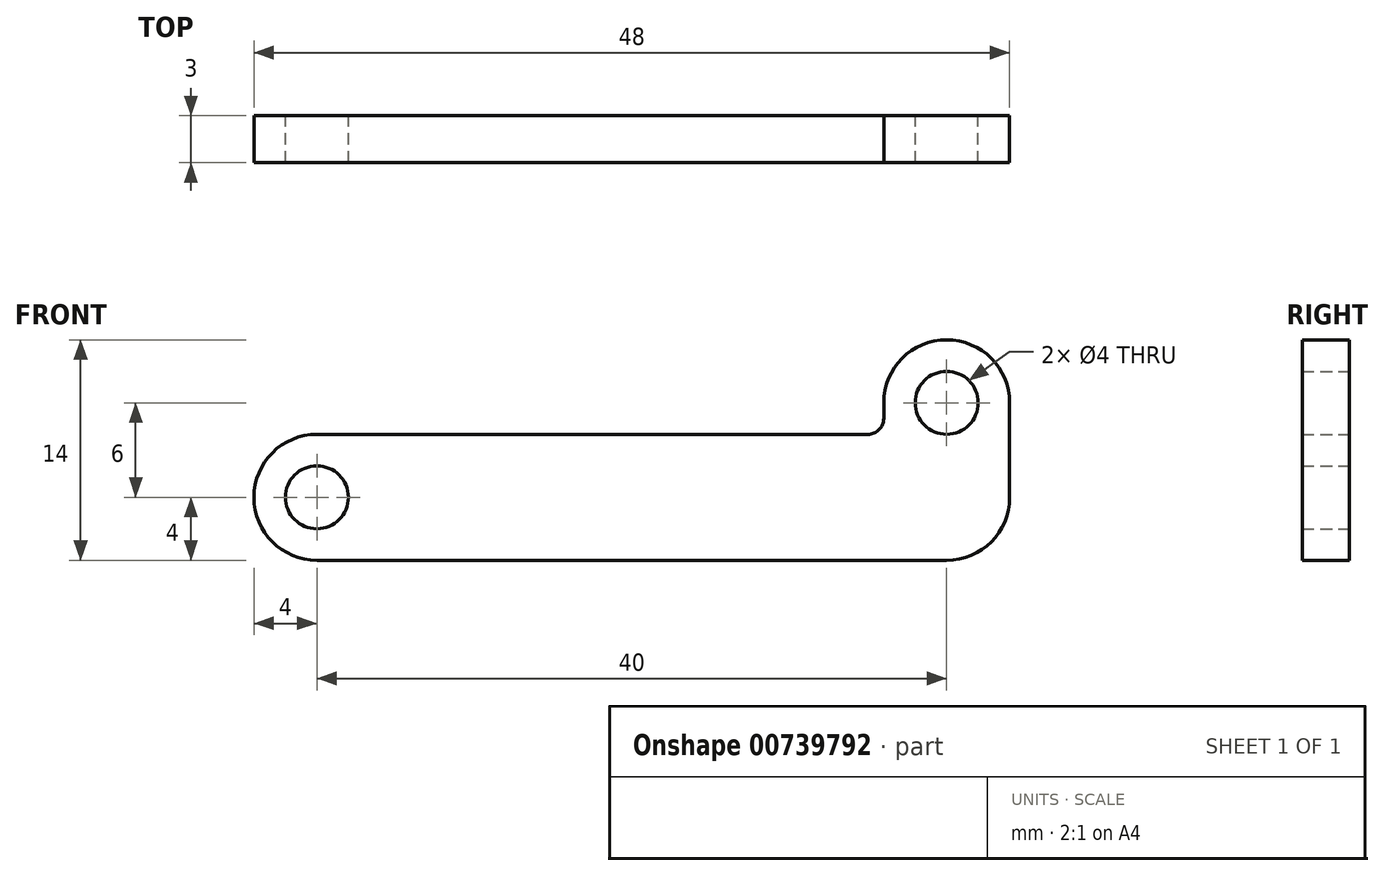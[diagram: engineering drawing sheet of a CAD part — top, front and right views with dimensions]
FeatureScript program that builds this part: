
annotation { "Feature Type Name" : "Feature", "Feature Type Description" : "" }
export const myFeature = defineFeature(function(context is Context, id is Id, definition is map)
    precondition{}
    {
        {
            var Q0;
            Q0=qCreatedBy(makeId("Front.planeOp"),FACE);
            var sketch = newSketch(context, id + "F0", { "sketchPlane" : qUnion([Q0])});
            skLineSegment(sketch, "E0.bottom", {"start": v(-40, 4) * mm, "end": v(-5, 4) * mm});
            skLineSegment(sketch, "E0.top", {"start": v(-40, -4) * mm, "end": v(4, -4) * mm});
            skLineSegment(sketch, "E0.left", {"start": v(-40, 4) * mm, "end": v(-40, -4) * mm, "construction": true});
            skLineSegment(sketch, "E1.bottom", {"start": v(0, -4) * mm, "end": v(-4, -4) * mm});
            skLineSegment(sketch, "E1.top", {"start": v(4, 6) * mm, "end": v(-4, 6) * mm, "construction": true});
            skLineSegment(sketch, "E1.left", {"start": v(4, 4) * mm, "end": v(4, 6) * mm});
            skLineSegment(sketch, "E1.right", {"start": v(-4, 5) * mm, "end": v(-4, 6) * mm});
            skLineSegment(sketch, "E2", {"start": v(4, 4) * mm, "end": v(4, 0) * mm});
            skArc(sketch, "E3", {"start": v(4, 6) * mm, "mid": v(0, 10) * mm, "end": v(-4, 6) * mm});
            skArc(sketch, "E4", {"start": v(-40, 4) * mm, "mid": v(-44, 0) * mm, "end": v(-40, -4) * mm});
            skPoint(sketch, "E5.visualSharp", {"position": v(-4, 4) * mm});
            skArc(sketch, "E5.filletArc", {"start": v(-5, 4) * mm, "mid": v(-4.3, 4.3) * mm, "end": v(-4, 5) * mm});
            skPoint(sketch, "E6.visualSharp", {"position": v(4, -4) * mm});
            skArc(sketch, "E6.filletArc", {"start": v(0, -4) * mm, "mid": v(2.83, -2.83) * mm, "end": v(4, 0) * mm});
            skCircle(sketch, "E7", {"center": v(0, 6) * mm, "radius": 2 * mm});
            skCircle(sketch, "E8", {"center": v(-40, 0) * mm, "radius": 2 * mm});
            skSolve(sketch);
        }
        {
            var Q0;
            Q0 = qSketchRegion(id + "F0", true);
            extrude(context, id + "F1", {"entities" : qUnion([Q0]), "depth" : 3 * mm, "offsetDistance" : 25 * mm});
        }
    });
